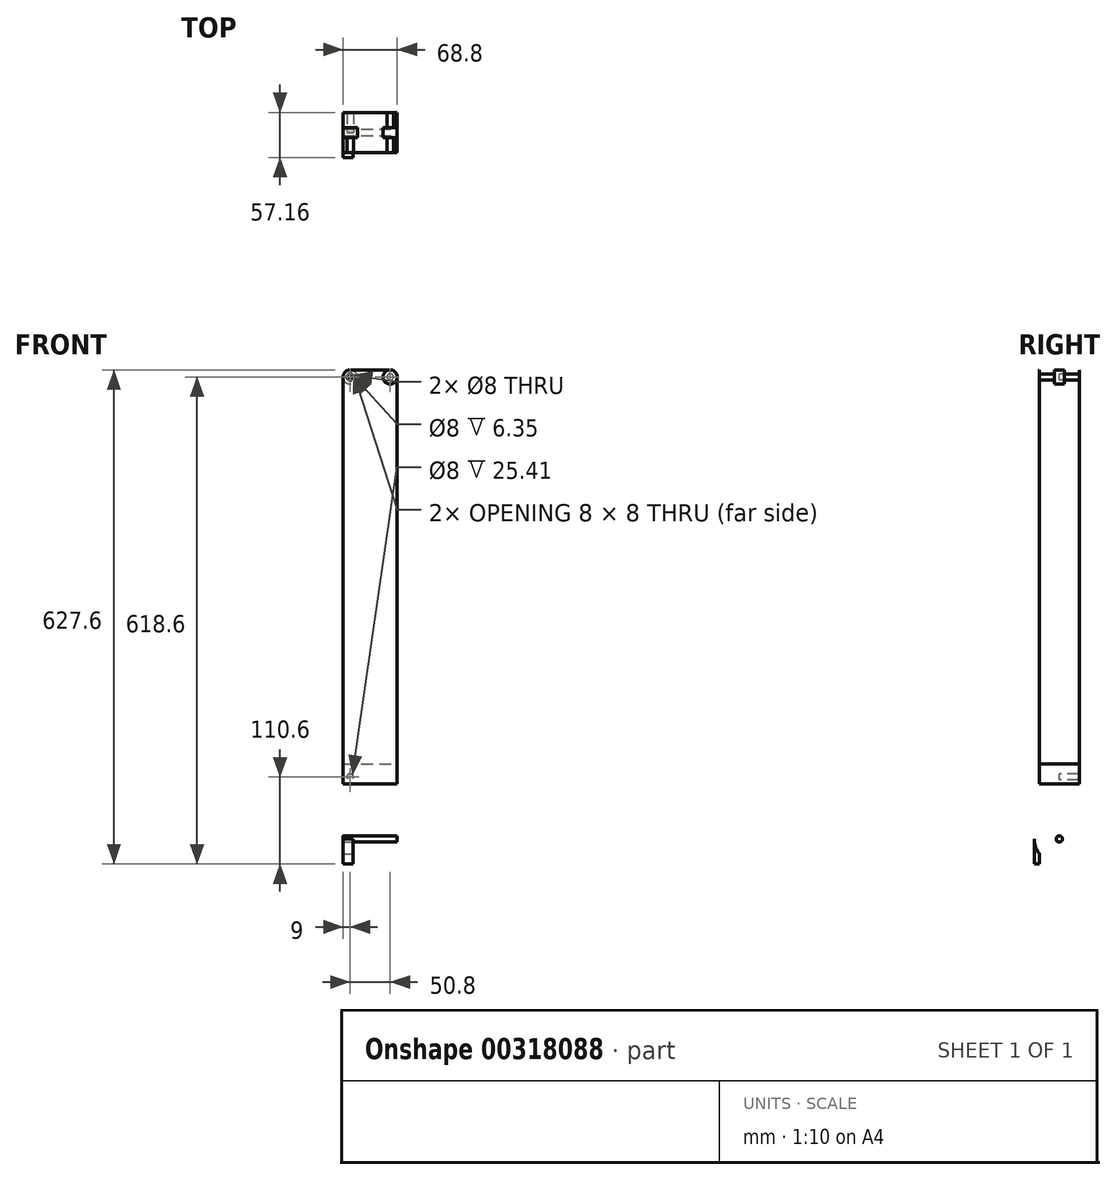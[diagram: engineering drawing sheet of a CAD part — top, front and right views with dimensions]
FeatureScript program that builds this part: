
annotation { "Feature Type Name" : "Feature", "Feature Type Description" : "" }
export const myFeature = defineFeature(function(context is Context, id is Id, definition is map)
    precondition{}
    {
        {
            var Q0;
            Q0=qCreatedBy(makeId("Front.planeOp"),FACE);
            var sketch = newSketch(context, id + "F0", { "sketchPlane" : qUnion([Q0])});
            skCircle(sketch, "E0", {"center": v(0, 0) * mm, "radius": 4 * mm});
            skCircle(sketch, "E1.0", {"center": v(0, 0) * mm, "radius": 9 * mm});
            skLineSegment(sketch, "E2", {"start": v(0, 508) * mm, "end": v(0, 0) * mm, "construction": true});
            skCircle(sketch, "E3", {"center": v(0, 508) * mm, "radius": 4 * mm});
            skCircle(sketch, "E4.0", {"center": v(0, 508) * mm, "radius": 9 * mm});
            skArc(sketch, "E5.0", {"start": v(9, 508) * mm, "mid": v(0, 517) * mm, "end": v(-9, 508) * mm, "construction": true});
            skLineSegment(sketch, "E6", {"start": v(-9, 508) * mm, "end": v(-9, 0) * mm});
            skLineSegment(sketch, "E7", {"start": v(9, 508) * mm, "end": v(9, 0) * mm});
            skLineSegment(sketch, "E8", {"start": v(25.4, 609) * mm, "end": v(25.4, 549.32) * mm, "construction": true});
            skCircle(sketch, "E9.MirrorC", {"center": v(50.8, 0) * mm, "radius": 4 * mm});
            skCircle(sketch, "E10.MirrorC", {"center": v(50.8, 508) * mm, "radius": 4 * mm});
            skCircle(sketch, "E11.MirrorC", {"center": v(50.8, 0) * mm, "radius": 9 * mm});
            skArc(sketch, "E12.MirrorCS", {"start": v(41.8, 508) * mm, "mid": v(50.8, 517) * mm, "end": v(59.8, 508) * mm, "construction": true});
            skCircle(sketch, "E13.MirrorC", {"center": v(50.8, 508) * mm, "radius": 9 * mm});
            skLineSegment(sketch, "E14.MirrorCS", {"start": v(59.8, 508) * mm, "end": v(59.8, 0) * mm});
            skLineSegment(sketch, "E15.MirrorCS", {"start": v(41.8, 508) * mm, "end": v(41.8, 0) * mm});
            skLineSegment(sketch, "E16.MirrorCS", {"start": v(50.8, 508) * mm, "end": v(50.8, 0) * mm, "construction": true});
            skLineSegment(sketch, "E17", {"start": v(0, 517) * mm, "end": v(50.8, 517) * mm});
            skLineSegment(sketch, "E18", {"start": v(0, -9) * mm, "end": v(50.8, -9) * mm});
            skLineSegment(sketch, "E19", {"start": v(-9, -9) * mm, "end": v(59.8, -9) * mm});
            skLineSegment(sketch, "E20", {"start": v(-9, 5.68) * mm, "end": v(-9, -9) * mm});
            skLineSegment(sketch, "E21", {"start": v(59.8, 8.13) * mm, "end": v(59.8, -9) * mm});
            skSolve(sketch);
        }
        {
            var Q0;
            Q0=qSketchRegion(id+"F0",true);
            var Q1;
            Q1=makeQuery(id+"F0.imprint","IMPRINT",FACE,{"disambiguationData":[TD([[makeQuery(id+"F0.imprint","IMPRINT",EDGE,{"derivedFrom":sQuery(id+"F0.wireOp",EDGE,"E10.MirrorC")}),1.0]])]});
            var Q2;
            Q2=makeQuery(id+"F0.imprint","IMPRINT",FACE,{"disambiguationData":[TD([[makeQuery(id+"F0.imprint","IMPRINT",EDGE,{"derivedFrom":sQuery(id+"F0.wireOp",EDGE,"E3")}),-1.0]])]});
            var Q3;
            Q3=makeQuery(id+"F0.imprint","IMPRINT",FACE,{"disambiguationData":[TD([[makeQuery(id+"F0.imprint","IMPRINT",EDGE,{"derivedFrom":sQuery(id+"F0.wireOp",EDGE,"E9.MirrorC")}),1.0]])]});
            var Q4;
            Q4=makeQuery(id+"F0.imprint","IMPRINT",FACE,{"disambiguationData":[TD([[makeQuery(id+"F0.imprint","IMPRINT",EDGE,{"derivedFrom":sQuery(id+"F0.wireOp",EDGE,"E0")}),-1.0]])]});
            var Q5;
            Q5 = qSketchRegion(id + "F2", true);
            extrude(context, id + "F1", {"entities" : qUnion([Q0, Q1, Q2, Q3, Q4, Q5]), "depth" : 1 / 101.6 * mm});
        }
        {
            var Q0;
            Q0=makeQuery(id+"F1.opExtrude","CAP_FACE",FACE,{"disambiguationData":[OSD([sQuery(id+"F0.wireOp",EDGE,"E1.0"),sQuery(id+"F0.wireOp",EDGE,"E4.0"),sQuery(id+"F0.wireOp",EDGE,"E6"),sQuery(id+"F0.wireOp",EDGE,"E11.MirrorC"),sQuery(id+"F0.wireOp",EDGE,"E14.MirrorCS"),sQuery(id+"F0.wireOp",EDGE,"E13.MirrorC"),sQuery(id+"F0.wireOp",EDGE,"E17"),sQuery(id+"F0.wireOp",EDGE,"E18")])],"isStart":true});
            var sketch = newSketch(context, id + "F2", { "sketchPlane" : qUnion([Q0])});
            skCircle(sketch, "E22.0", {"center": v(-50.8, 508) * mm, "radius": 4 * mm});
            skCircle(sketch, "E23.0", {"center": v(0, 508) * mm, "radius": 4 * mm});
            skSolve(sketch);
        }
        {
            var Q0;
            Q0 = qSketchRegion(id + "F2", true);
            var Q1;
            Q1=makeQuery(id+"F0.imprint","IMPRINT",FACE,{"disambiguationData":[TD([[makeQuery(id+"F0.imprint","IMPRINT",EDGE,{"derivedFrom":sQuery(id+"F0.wireOp",EDGE,"E10.MirrorC")}),1.0]])]});
            extrude(context, id + "F3", {"entities" : qUnion([Q0, Q1]), "operationType" : NewBodyOperationType.ADD, "depth" : 25.4 * mm});
        }
        {
            var Q0;
            {var subQ0=sQuery(id+"F0.wireOp",EDGE,"E7");Q0=makeQuery(id+"F0.imprint","IMPRINT",FACE,{"disambiguationData":[TD([[makeQuery(id+"F0.imprint","IMPRINT",EDGE,{"derivedFrom":subQ0}),1.0]])]});}
            var sketch = newSketch(context, id + "F4", { "sketchPlane" : qUnion([Q0])});
            skCircle(sketch, "E24.0", {"center": v(0, 0) * mm, "radius": 4 * mm});
            skCircle(sketch, "E25.0", {"center": v(50.8, 0) * mm, "radius": 4 * mm});
            skSolve(sketch);
        }
        {
            var Q0;
            Q0 = qSketchRegion(id + "F4", true);
            extrude(context, id + "F5", {"entities" : qUnion([Q0]), "operationType" : NewBodyOperationType.ADD, "oppositeDirection" : true, "depth" : 25.4 * mm});
        }
        {
            var Q0;
            Q0=makeQuery(id+"F0.imprint","IMPRINT",FACE,{"disambiguationData":[TD([[makeQuery(id+"F0.imprint","IMPRINT",EDGE,{"derivedFrom":sQuery(id+"F0.wireOp",EDGE,"E0")}),1.0]])]});
            var Q1;
            Q1=makeQuery(id+"F0.imprint","IMPRINT",FACE,{"disambiguationData":[TD([[makeQuery(id+"F0.imprint","IMPRINT",EDGE,{"derivedFrom":sQuery(id+"F0.wireOp",EDGE,"E9.MirrorC")}),-1.0]])]});
            var Q2;
            Q2=makeQuery(id+"F0.imprint","IMPRINT",FACE,{"disambiguationData":[TD([[makeQuery(id+"F0.imprint","IMPRINT",EDGE,{"derivedFrom":sQuery(id+"F0.wireOp",EDGE,"E3")}),1.0]])]});
            var Q3;
            Q3=makeQuery(id+"F0.imprint","IMPRINT",FACE,{"disambiguationData":[TD([[makeQuery(id+"F0.imprint","IMPRINT",EDGE,{"derivedFrom":sQuery(id+"F0.wireOp",EDGE,"E10.MirrorC")}),-1.0]])]});
            extrude(context, id + "F6", {"entities" : qUnion([Q0, Q1, Q2, Q3]), "operationType" : NewBodyOperationType.ADD, "oppositeDirection" : true, "depth" : 1 / 101.6 * mm});
        }
        {
            var Q0;
            Q0=makeQuery(id+"F3.opExtrude","CAP_FACE",FACE,{"disambiguationData":[OSD([sQuery(id+"F2.wireOp",EDGE,"E23.0")])],"isStart":false});
            cPlane(context, id + "F7", {"entities" : qUnion([Q0]), "cplaneType" : CPlaneType.OFFSET, "offset" : 0 * mm, "width" : 150 * mm, "height" : 150 * mm});
        }
        {
            var Q0;
            Q0=makeQuery(id+"F1.opExtrude","SWEPT_BODY",BODY,{"disambiguationData":[OSD([sQuery(id+"F0.wireOp",EDGE,"E1.0"),sQuery(id+"F0.wireOp",EDGE,"E4.0"),sQuery(id+"F0.wireOp",EDGE,"E6"),sQuery(id+"F0.wireOp",EDGE,"E11.MirrorC"),sQuery(id+"F0.wireOp",EDGE,"E14.MirrorCS"),sQuery(id+"F0.wireOp",EDGE,"E13.MirrorC"),sQuery(id+"F0.wireOp",EDGE,"E17"),sQuery(id+"F0.wireOp",EDGE,"E18")])]});
            var Q1;
            Q1=qCreatedBy(id+"F7.planeOp",FACE);
            mirror(context, id + "F8", {"operationType" : NewBodyOperationType.ADD, "entities" : qUnion([Q0]), "mirrorPlane" : qUnion([Q1])});
        }
        {
            var Q0;
            Q0=makeQuery(id+"F1.opExtrude","CAP_FACE",FACE,{"disambiguationData":[OSD([sQuery(id+"F0.wireOp",EDGE,"E4.0"),sQuery(id+"F0.wireOp",EDGE,"E6"),sQuery(id+"F0.wireOp",EDGE,"E14.MirrorCS"),sQuery(id+"F0.wireOp",EDGE,"E13.MirrorC"),sQuery(id+"F0.wireOp",EDGE,"E17"),sQuery(id+"F0.wireOp",EDGE,"E19"),sQuery(id+"F0.wireOp",EDGE,"E20"),sQuery(id+"F0.wireOp",EDGE,"E21")])],"isStart":false});
            var sketch = newSketch(context, id + "F9", { "sketchPlane" : qUnion([Q0])});
            skLineSegment(sketch, "E26.bottom", {"start": v(-9, -9) * mm, "end": v(59.8, -9) * mm});
            skLineSegment(sketch, "E26.top", {"start": v(-9, 16.4) * mm, "end": v(59.8, 16.4) * mm});
            skLineSegment(sketch, "E26.left", {"start": v(-9, -9) * mm, "end": v(-9, 16.4) * mm});
            skLineSegment(sketch, "E26.right", {"start": v(59.8, -9) * mm, "end": v(59.8, 16.4) * mm});
            skSolve(sketch);
        }
        {
            var Q0;
            Q0=makeQuery(id+"F9.imprint","IMPRINT",FACE,{"disambiguationData":[TD([[makeQuery(id+"F9.imprint","IMPRINT",EDGE,{"derivedFrom":sQuery(id+"F9.wireOp",EDGE,"E26.bottom")}),1.0]])]});
            var Q1;
            {var subQ0=sQuery(id+"F0.wireOp",EDGE,"E19");var subQ1=sQuery(id+"F0.wireOp",EDGE,"E17");var subQ2=sQuery(id+"F0.wireOp",EDGE,"E13.MirrorC");var subQ3=sQuery(id+"F0.wireOp",EDGE,"E4.0");var subQ4=sQuery(id+"F0.wireOp",EDGE,"E21");var subQ5=sQuery(id+"F0.wireOp",EDGE,"E20");var subQ6=sQuery(id+"F0.wireOp",EDGE,"E14.MirrorCS");var subQ7=sQuery(id+"F0.wireOp",EDGE,"E6");var subQ8=makeQuery(id+"F1.opExtrude","CAP_FACE",FACE,{"disambiguationData":[OSD([subQ3,subQ7,subQ6,subQ2,subQ1,subQ0,subQ5,subQ4])],"isStart":true});Q1=makeQuery(id+"F8.opPattern","COPY",FACE,{"derivedFrom":makeQuery(id+"F6.boolean.opBoolean","SPLIT",FACE,{"disambiguationData":[TD([makeQuery(id+"F1.opExtrude","SWEPT_FACE",FACE,{"disambiguationData":[OSD([subQ3])]}),subQ8,makeQuery(id+"F1.opExtrude","SWEPT_FACE",FACE,{"disambiguationData":[OSD([subQ7,subQ5])]}),makeQuery(id+"F1.opExtrude","SWEPT_FACE",FACE,{"disambiguationData":[OSD([subQ6,subQ4])]}),makeQuery(id+"F1.opExtrude","SWEPT_FACE",FACE,{"disambiguationData":[OSD([subQ2])]}),makeQuery(id+"F1.opExtrude","SWEPT_FACE",FACE,{"disambiguationData":[OSD([subQ1])]}),makeQuery(id+"F1.opExtrude","SWEPT_FACE",FACE,{"disambiguationData":[OSD([subQ0])]}),makeQuery(id+"F6.opExtrude","SWEPT_FACE",FACE,{"disambiguationData":[OSD([sQuery(id+"F0.wireOp",EDGE,"E1.0")])]}),makeQuery(id+"F6.opExtrude","SWEPT_FACE",FACE,{"disambiguationData":[OSD([subQ3])]}),makeQuery(id+"F6.opExtrude","SWEPT_FACE",FACE,{"disambiguationData":[OSD([sQuery(id+"F0.wireOp",EDGE,"E11.MirrorC")])]}),makeQuery(id+"F6.opExtrude","SWEPT_FACE",FACE,{"disambiguationData":[OSD([subQ2])]})])],"derivedFrom":subQ8}),"instanceName":"1"});}
            extrude(context, id + "F10", {"entities" : qUnion([Q0]), "operationType" : NewBodyOperationType.ADD, "endBound" : BoundingType.UP_TO_SURFACE, "oppositeDirection" : true, "endBoundEntityFace" : qUnion([Q1]), "depth" : 25 * mm});
        }
        {
            var Q0;
            {var subQ0=makeQuery(id+"F1.opExtrude","SWEPT_FACE",FACE,{"disambiguationData":[OSD([sQuery(id+"F0.wireOp",EDGE,"E19")])]});Q0=makeQuery(id+"F10.boolean.opBoolean","MERGE",FACE,{"derivedFrom":[subQ0,makeQuery(id+"F8.opPattern","COPY",FACE,{"derivedFrom":subQ0,"instanceName":"1"}),makeQuery(id+"F10.opExtrude","SWEPT_FACE",FACE,{"disambiguationData":[OSD([sQuery(id+"F9.wireOp",EDGE,"E26.bottom")])]})]});}
            var sketch = newSketch(context, id + "F11", { "sketchPlane" : qUnion([Q0])});
            skLineSegment(sketch, "E27.bottom", {"start": v(-9, 6.35) * mm, "end": v(3.7, 6.35) * mm});
            skLineSegment(sketch, "E27.top", {"start": v(-9, -57.15) * mm, "end": v(3.7, -57.15) * mm});
            skLineSegment(sketch, "E27.left", {"start": v(-9, 6.35) * mm, "end": v(-9, -57.15) * mm});
            skLineSegment(sketch, "E27.right", {"start": v(3.7, 6.35) * mm, "end": v(3.7, -57.15) * mm});
            skLineSegment(sketch, "E28.bottom", {"start": v(59.8, 6.35) * mm, "end": v(47.1, 6.35) * mm});
            skLineSegment(sketch, "E28.top", {"start": v(59.8, -57.15) * mm, "end": v(47.1, -57.15) * mm});
            skLineSegment(sketch, "E28.left", {"start": v(59.8, 6.35) * mm, "end": v(59.8, -57.15) * mm});
            skLineSegment(sketch, "E28.right", {"start": v(47.1, 6.35) * mm, "end": v(47.1, -57.15) * mm});
            skSolve(sketch);
        }
        {
            var Q0;
            Q0=makeQuery(id+"F11.imprint","IMPRINT",FACE,{"disambiguationData":[TD([[makeQuery(id+"F11.imprint","IMPRINT",EDGE,{"derivedFrom":sQuery(id+"F11.wireOp",EDGE,"E27.bottom")}),-1.0]])]});
            var Q1;
            Q1=makeQuery(id+"F11.imprint","IMPRINT",FACE,{"disambiguationData":[TD([[makeQuery(id+"F11.imprint","IMPRINT",EDGE,{"derivedFrom":sQuery(id+"F11.wireOp",EDGE,"E28.bottom")}),-1.0]])]});
            extrude(context, id + "F12", {"entities" : qUnion([Q0, Q1]), "operationType" : NewBodyOperationType.ADD, "depth" : 101.6 * mm});
        }
        {
            var Q0;
            Q0=makeQuery(id+"F12.opExtrude","SWEPT_FACE",FACE,{"disambiguationData":[OSD([sQuery(id+"F11.wireOp",EDGE,"E27.right")])]});
            var sketch = newSketch(context, id + "F13", { "sketchPlane" : qUnion([Q0])});
            skLineSegment(sketch, "E29.0", {"start": v(-6.35, 508) * mm, "end": v(-6.35, -90.6) * mm});
            skLineSegment(sketch, "E30.0", {"start": v(13.65, -110.6) * mm, "end": v(57.15, -110.6) * mm});
            skLineSegment(sketch, "E31.0", {"start": v(57.15, 508) * mm, "end": v(57.15, -110.6) * mm});
            skPoint(sketch, "E32.visualSharp", {"position": v(-6.35, -110.6) * mm});
            skArc(sketch, "E33", {"start": v(-6.35, -78.85) * mm, "mid": v(25.4, -110.6) * mm, "end": v(57.15, -78.85) * mm});
            skPoint(sketch, "E33.first.point", {"position": v(-6.35, -78.85) * mm});
            skPoint(sketch, "E33.second.point", {"position": v(25.4, -110.6) * mm});
            skPoint(sketch, "E33.third.point", {"position": v(57.15, -78.85) * mm});
            skSolve(sketch);
        }
        {
            var Q0;
            {var subQ0=sQuery(id+"F13.wireOp",EDGE,"E29.0");var subQ1=makeQuery(id+"F12.opExtrude","CAP_EDGE",EDGE,{"disambiguationData":[OSD([sQuery(id+"F11.wireOp",EDGE,"E27.right")])],"isStart":false});var subQ2=makeQuery(id+"F13.imprint","INTERSECT",VERTEX,{"derivedFrom":[subQ1,subQ0]});Q0=makeQuery(id+"F13.imprint","IMPRINT",FACE,{"disambiguationData":[TD([[makeQuery(id+"F13.imprint","IMPRINT",EDGE,{"disambiguationData":[TD([[subQ2,-1.0]])],"derivedFrom":subQ0}),-1.0]])]});}
            var Q1;
            {var subQ0=sQuery(id+"F13.wireOp",EDGE,"E31.0");var subQ1=sQuery(id+"F13.wireOp",EDGE,"E30.0");var subQ2=makeQuery(id+"F13.imprint","INTERSECT",VERTEX,{"derivedFrom":[subQ1,subQ0]});Q1=makeQuery(id+"F13.imprint","IMPRINT",FACE,{"disambiguationData":[TD([[makeQuery(id+"F13.imprint","IMPRINT",EDGE,{"disambiguationData":[TD([[subQ2,1.0]])],"derivedFrom":subQ1}),1.0]])]});}
            extrude(context, id + "F14", {"entities" : qUnion([Q0, Q1]), "operationType" : NewBodyOperationType.REMOVE, "oppositeDirection" : true, "depth" : 25 * mm, "hasSecondDirection" : true, "secondDirectionBound" : SecondDirectionBoundingType.THROUGH_ALL, "secondDirectionOppositeDirection" : false, "secondDirectionDepth" : 25 * mm});
        }
        {
            var Q0;
            {var subQ0=makeQuery(id+"F1.opExtrude","SWEPT_FACE",FACE,{"disambiguationData":[OSD([sQuery(id+"F0.wireOp",EDGE,"E14.MirrorCS"),sQuery(id+"F0.wireOp",EDGE,"E21")])]});Q0=makeQuery(id+"F12.boolean.opBoolean","MERGE",FACE,{"derivedFrom":[makeQuery(id+"F10.boolean.opBoolean","MERGE",FACE,{"derivedFrom":[subQ0,makeQuery(id+"F8.opPattern","COPY",FACE,{"derivedFrom":subQ0,"instanceName":"1"}),makeQuery(id+"F10.opExtrude","SWEPT_FACE",FACE,{"disambiguationData":[OSD([sQuery(id+"F9.wireOp",EDGE,"E26.right")])]})]}),makeQuery(id+"F12.opExtrude","SWEPT_FACE",FACE,{"disambiguationData":[OSD([sQuery(id+"F11.wireOp",EDGE,"E28.left")])]})]});}
            var sketch = newSketch(context, id + "F15", { "sketchPlane" : qUnion([Q0])});
            skPoint(sketch, "E34.0", {"position": v(25.4, -78.85) * mm});
            skCircle(sketch, "E35", {"center": v(25.4, -78.85) * mm, "radius": 4 * mm});
            skSolve(sketch);
        }
        {
            var Q0;
            Q0 = qSketchRegion(id + "F15", true);
            var Q1;
            {var subQ0=makeQuery(id+"F1.opExtrude","SWEPT_FACE",FACE,{"disambiguationData":[OSD([sQuery(id+"F0.wireOp",EDGE,"E6"),sQuery(id+"F0.wireOp",EDGE,"E20")])]});Q1=makeQuery(id+"F12.boolean.opBoolean","MERGE",FACE,{"derivedFrom":[makeQuery(id+"F10.boolean.opBoolean","MERGE",FACE,{"derivedFrom":[subQ0,makeQuery(id+"F8.opPattern","COPY",FACE,{"derivedFrom":subQ0,"instanceName":"1"}),makeQuery(id+"F10.opExtrude","SWEPT_FACE",FACE,{"disambiguationData":[OSD([sQuery(id+"F9.wireOp",EDGE,"E26.left")])]})]}),makeQuery(id+"F12.opExtrude","SWEPT_FACE",FACE,{"disambiguationData":[OSD([sQuery(id+"F11.wireOp",EDGE,"E27.left")])]})]});}
            extrude(context, id + "F16", {"entities" : qUnion([Q0]), "operationType" : NewBodyOperationType.ADD, "endBound" : BoundingType.UP_TO_SURFACE, "oppositeDirection" : true, "endBoundEntityFace" : qUnion([Q1]), "depth" : 25 * mm});
        }
        {
            var Q0;
            Q0=qCreatedBy(id+"F7.planeOp",FACE);
            var sketch = newSketch(context, id + "F17", { "sketchPlane" : qUnion([Q0])});
            skCircle(sketch, "E36.0", {"center": v(0, 508) * mm, "radius": 4 * mm});
            skCircle(sketch, "E37.0", {"center": v(0, 508) * mm, "radius": 9 * mm});
            skCircle(sketch, "E38.0", {"center": v(-50.8, 508) * mm, "radius": 4 * mm});
            skCircle(sketch, "E39.0", {"center": v(-50.8, 508) * mm, "radius": 9 * mm});
            skSolve(sketch);
        }
        {
            var Q0;
            Q0 = qSketchRegion(id + "F17", true);
            extrude(context, id + "F18", {"entities" : qUnion([Q0]), "operationType" : NewBodyOperationType.ADD, "depth" : 6.35 * mm, "hasSecondDirection" : true, "secondDirectionOppositeDirection" : true, "secondDirectionDepth" : 6.35 * mm});
        }
        {
            var Q0;
            {var subQ0=makeQuery(id+"F1.opExtrude","SWEPT_FACE",FACE,{"disambiguationData":[OSD([sQuery(id+"F0.wireOp",EDGE,"E14.MirrorCS"),sQuery(id+"F0.wireOp",EDGE,"E21")])]});Q0=makeQuery(id+"F12.boolean.opBoolean","MERGE",FACE,{"derivedFrom":[makeQuery(id+"F10.boolean.opBoolean","MERGE",FACE,{"derivedFrom":[subQ0,makeQuery(id+"F8.opPattern","COPY",FACE,{"derivedFrom":subQ0,"instanceName":"1"}),makeQuery(id+"F10.opExtrude","SWEPT_FACE",FACE,{"disambiguationData":[OSD([sQuery(id+"F9.wireOp",EDGE,"E26.right")])]})]}),makeQuery(id+"F12.opExtrude","SWEPT_FACE",FACE,{"disambiguationData":[OSD([sQuery(id+"F11.wireOp",EDGE,"E28.left")])]})]});}
            var sketch = newSketch(context, id + "F19", { "sketchPlane" : qUnion([Q0])});
            skLineSegment(sketch, "E40.0.0", {"start": v(57.15, -9) * mm, "end": v(50.8, -9) * mm});
            skLineSegment(sketch, "E40.0.2", {"start": v(-6.35, -9) * mm, "end": v(0, -9) * mm});
            skLineSegment(sketch, "E41", {"start": v(50.8, 16.4) * mm, "end": v(50.8, -9) * mm});
            skLineSegment(sketch, "E42", {"start": v(0, 16.4) * mm, "end": v(0, -9) * mm});
            skLineSegment(sketch, "E43.trimOffspring", {"start": v(50.8, -9) * mm, "end": v(57.15, -9) * mm});
            skLineSegment(sketch, "E44.trimOffspring", {"start": v(0, -9) * mm, "end": v(-6.35, -9) * mm});
            skSolve(sketch);
        }
        {
            var Q0;
            Q0 = qSketchRegion(id + "F19", true);
            var Q1;
            Q1=sQuery(id+"F19.wireOp",EDGE,"E42");
            var Q2;
            Q2=sQuery(id+"F19.wireOp",EDGE,"E40.0.2");
            var Q3;
            {var subQ0=makeQuery(id+"F1.opExtrude","SWEPT_FACE",FACE,{"disambiguationData":[OSD([sQuery(id+"F0.wireOp",EDGE,"E6"),sQuery(id+"F0.wireOp",EDGE,"E20")])]});Q3=makeQuery(id+"F12.boolean.opBoolean","MERGE",FACE,{"derivedFrom":[makeQuery(id+"F10.boolean.opBoolean","MERGE",FACE,{"derivedFrom":[subQ0,makeQuery(id+"F8.opPattern","COPY",FACE,{"derivedFrom":subQ0,"instanceName":"1"}),makeQuery(id+"F10.opExtrude","SWEPT_FACE",FACE,{"disambiguationData":[OSD([sQuery(id+"F9.wireOp",EDGE,"E26.left")])]})]}),makeQuery(id+"F12.opExtrude","SWEPT_FACE",FACE,{"disambiguationData":[OSD([sQuery(id+"F11.wireOp",EDGE,"E27.left")])]})]});}
            extrude(context, id + "F20", {"entities" : qUnion([Q0]), "bodyType" : ToolBodyType.SURFACE, "surfaceEntities" : qUnion([Q1, Q2]), "endBound" : BoundingType.UP_TO_SURFACE, "oppositeDirection" : true, "endBoundEntityFace" : qUnion([Q3]), "depth" : 25 * mm});
        }
        {
            var Q0;
            Q0=makeQuery(id+"F19.imprint","IMPRINT",FACE,{"disambiguationData":[TD([[makeQuery(id+"F19.imprint","IMPRINT",EDGE,{"derivedFrom":sQuery(id+"F19.wireOp",EDGE,"E41")}),1.0]])]});
            var Q1;
            Q1=sQuery(id+"F19.wireOp",EDGE,"E41");
            var Q2;
            Q2=sQuery(id+"F19.wireOp",EDGE,"E40.0.0");
            var Q3;
            {var subQ0=makeQuery(id+"F1.opExtrude","SWEPT_FACE",FACE,{"disambiguationData":[OSD([sQuery(id+"F0.wireOp",EDGE,"E6"),sQuery(id+"F0.wireOp",EDGE,"E20")])]});Q3=makeQuery(id+"F12.boolean.opBoolean","MERGE",FACE,{"derivedFrom":[makeQuery(id+"F10.boolean.opBoolean","MERGE",FACE,{"derivedFrom":[subQ0,makeQuery(id+"F8.opPattern","COPY",FACE,{"derivedFrom":subQ0,"instanceName":"1"}),makeQuery(id+"F10.opExtrude","SWEPT_FACE",FACE,{"disambiguationData":[OSD([sQuery(id+"F9.wireOp",EDGE,"E26.left")])]})]}),makeQuery(id+"F12.opExtrude","SWEPT_FACE",FACE,{"disambiguationData":[OSD([sQuery(id+"F11.wireOp",EDGE,"E27.left")])]})]});}
            extrude(context, id + "F21", {"entities" : qUnion([Q0]), "bodyType" : ToolBodyType.SURFACE, "surfaceEntities" : qUnion([Q1, Q2]), "endBound" : BoundingType.UP_TO_SURFACE, "oppositeDirection" : true, "endBoundEntityFace" : qUnion([Q3]), "depth" : 25 * mm});
        }
    });
